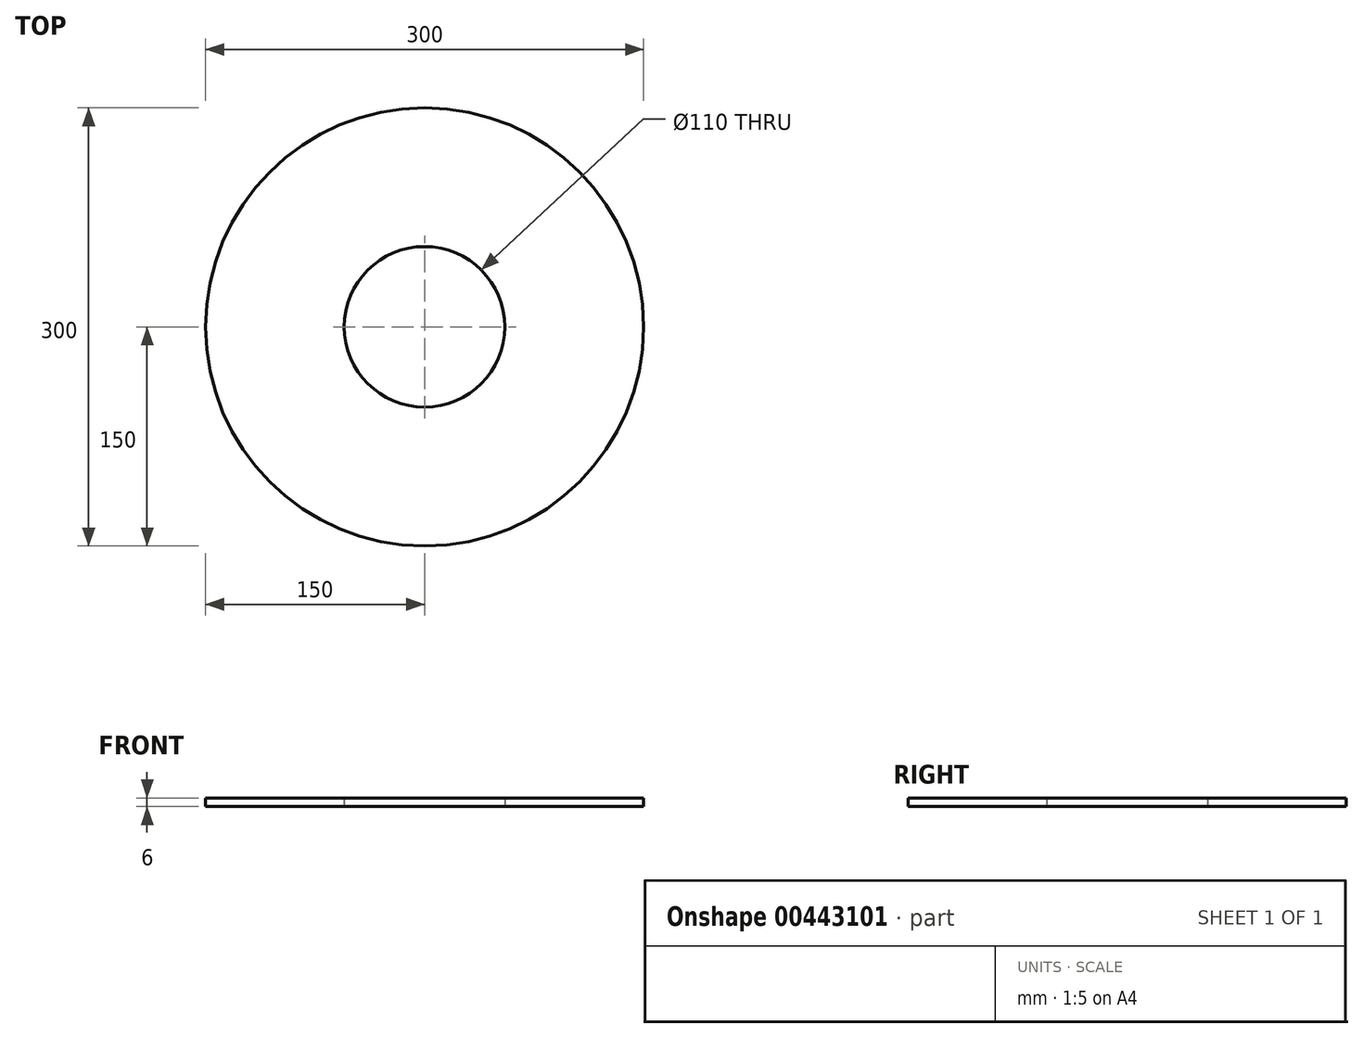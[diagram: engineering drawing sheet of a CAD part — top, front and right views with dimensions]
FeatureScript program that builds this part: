
annotation { "Feature Type Name" : "Feature", "Feature Type Description" : "" }
export const myFeature = defineFeature(function(context is Context, id is Id, definition is map)
    precondition{}
    {
        {
            var Q0;
            Q0=qCreatedBy(makeId("Top.planeOp"),FACE);
            var sketch = newSketch(context, id + "F0", { "sketchPlane" : qUnion([Q0])});
            skCircle(sketch, "E0", {"center": v(0, 0) * mm, "radius": 150 * mm});
            skCircle(sketch, "E1", {"center": v(0, 0) * mm, "radius": 55 * mm});
            skSolve(sketch);
        }
        {
            var Q0;
            Q0=makeQuery(id+"F0.imprint","IMPRINT",FACE,{"disambiguationData":[TD([[makeQuery(id+"F0.imprint","IMPRINT",EDGE,{"derivedFrom":sQuery(id+"F0.wireOp",EDGE,"E0")}),1.0]])]});
            extrude(context, id + "F1", {"entities" : qUnion([Q0]), "depth" : 6 * mm});
        }
    });
